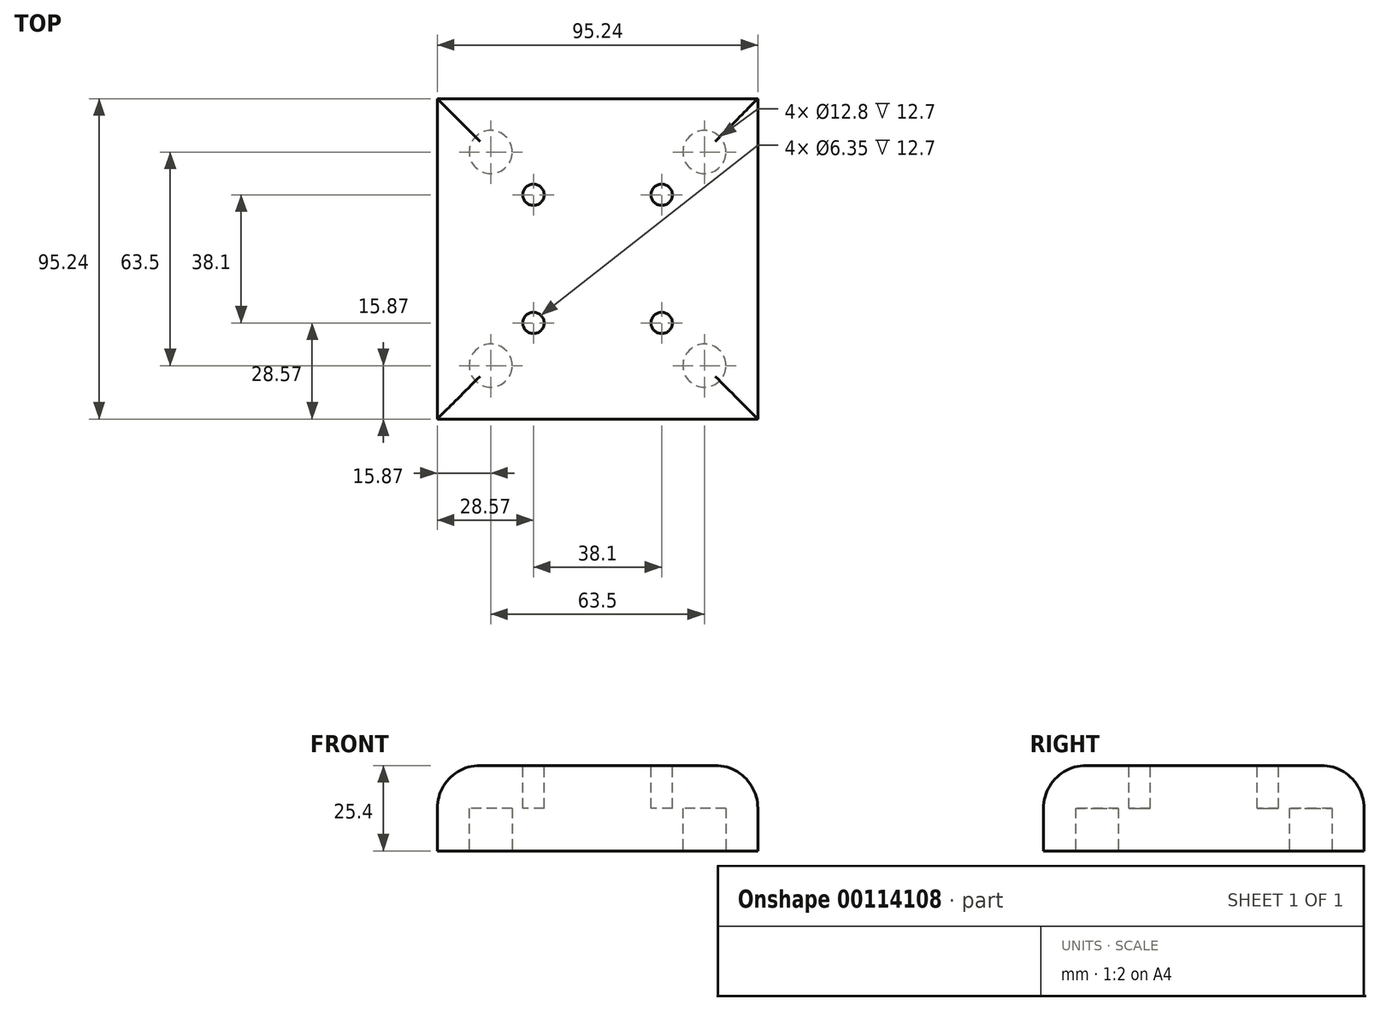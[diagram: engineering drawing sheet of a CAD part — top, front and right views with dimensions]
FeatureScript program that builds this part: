
annotation { "Feature Type Name" : "Feature", "Feature Type Description" : "" }
export const myFeature = defineFeature(function(context is Context, id is Id, definition is map)
    precondition{}
    {
        {
            var Q0;
            Q0=qCreatedBy(makeId("Top.planeOp"),FACE);
            var sketch = newSketch(context, id + "F0", { "sketchPlane" : qUnion([Q0])});
            skLineSegment(sketch, "E0.bottom", {"start": v(47.63, 47.63) * mm, "end": v(-47.63, 47.63) * mm});
            skLineSegment(sketch, "E0.top", {"start": v(47.63, -47.63) * mm, "end": v(-47.63, -47.63) * mm});
            skLineSegment(sketch, "E0.left", {"start": v(47.63, 47.63) * mm, "end": v(47.63, -47.63) * mm});
            skLineSegment(sketch, "E0.right", {"start": v(-47.63, 47.63) * mm, "end": v(-47.63, -47.63) * mm});
            skPoint(sketch, "E0.middle", {"position": v(0, 0) * mm});
            skSolve(sketch);
        }
        {
            var Q0;
            Q0=qCreatedBy(makeId("Top.planeOp"),FACE);
            var sketch = newSketch(context, id + "F1", { "sketchPlane" : qUnion([Q0])});
            skPoint(sketch, "E1.middle", {"position": v(0, 0) * mm});
            skCircle(sketch, "E2", {"center": v(-31.75, 31.75) * mm, "radius": 6.4 * mm});
            skCircle(sketch, "E3", {"center": v(31.75, 31.75) * mm, "radius": 6.4 * mm});
            skCircle(sketch, "E4", {"center": v(31.75, -31.75) * mm, "radius": 6.4 * mm});
            skCircle(sketch, "E5", {"center": v(-31.75, -31.75) * mm, "radius": 6.4 * mm});
            skSolve(sketch);
        }
        {
            var Q0;
            Q0 = qSketchRegion(id + "F0", true);
            extrude(context, id + "F2", {"entities" : qUnion([Q0]), "depth" : 25.4 * mm});
        }
        {
            var Q0;
            Q0 = qSketchRegion(id + "F1", true);
            extrude(context, id + "F3", {"entities" : qUnion([Q0]), "operationType" : NewBodyOperationType.REMOVE, "depth" : 12.7 * mm});
        }
        {
            var Q0;
            Q0=makeQuery(id+"F2.opExtrude","CAP_FACE",FACE,{"disambiguationData":[OSD([sQuery(id+"F0.wireOp",EDGE,"E0.bottom"),sQuery(id+"F0.wireOp",EDGE,"E0.top"),sQuery(id+"F0.wireOp",EDGE,"E0.left"),sQuery(id+"F0.wireOp",EDGE,"E0.right")])],"isStart":false});
            var sketch = newSketch(context, id + "F4", { "sketchPlane" : qUnion([Q0])});
            skCircle(sketch, "E6", {"center": v(-19.05, -19.05) * mm, "radius": 3.17 * mm});
            skCircle(sketch, "E7.1.0", {"center": v(19.05, -19.05) * mm, "radius": 3.17 * mm});
            skCircle(sketch, "E7.2.0", {"center": v(19.05, 19.05) * mm, "radius": 3.17 * mm});
            skCircle(sketch, "E7.3.0", {"center": v(-19.05, 19.05) * mm, "radius": 3.17 * mm});
            skPoint(sketch, "E7.center", {"position": v(0, 0) * mm});
            skSolve(sketch);
        }
        {
            var Q0;
            Q0 = qSketchRegion(id + "F4", true);
            extrude(context, id + "F5", {"entities" : qUnion([Q0]), "operationType" : NewBodyOperationType.REMOVE, "oppositeDirection" : true, "depth" : 12.7 * mm});
        }
        {
            var Q0;
            Q0=makeQuery(id+"F2.opExtrude","CAP_EDGE",EDGE,{"disambiguationData":[OSD([sQuery(id+"F0.wireOp",EDGE,"E0.right")])],"isStart":false});
            var Q1;
            Q1=makeQuery(id+"F2.opExtrude","CAP_EDGE",EDGE,{"disambiguationData":[OSD([sQuery(id+"F0.wireOp",EDGE,"E0.top")])],"isStart":false});
            var Q2;
            Q2=makeQuery(id+"F2.opExtrude","CAP_EDGE",EDGE,{"disambiguationData":[OSD([sQuery(id+"F0.wireOp",EDGE,"E0.left")])],"isStart":false});
            var Q3;
            Q3=makeQuery(id+"F2.opExtrude","CAP_EDGE",EDGE,{"disambiguationData":[OSD([sQuery(id+"F0.wireOp",EDGE,"E0.bottom")])],"isStart":false});
            fillet(context, id + "F6", {"entities" : qUnion([Q0, Q1, Q2, Q3]), "radius" : 12.7 * mm, "tangentPropagation" : true, "allowEdgeOverflow" : false});
        }
    });
